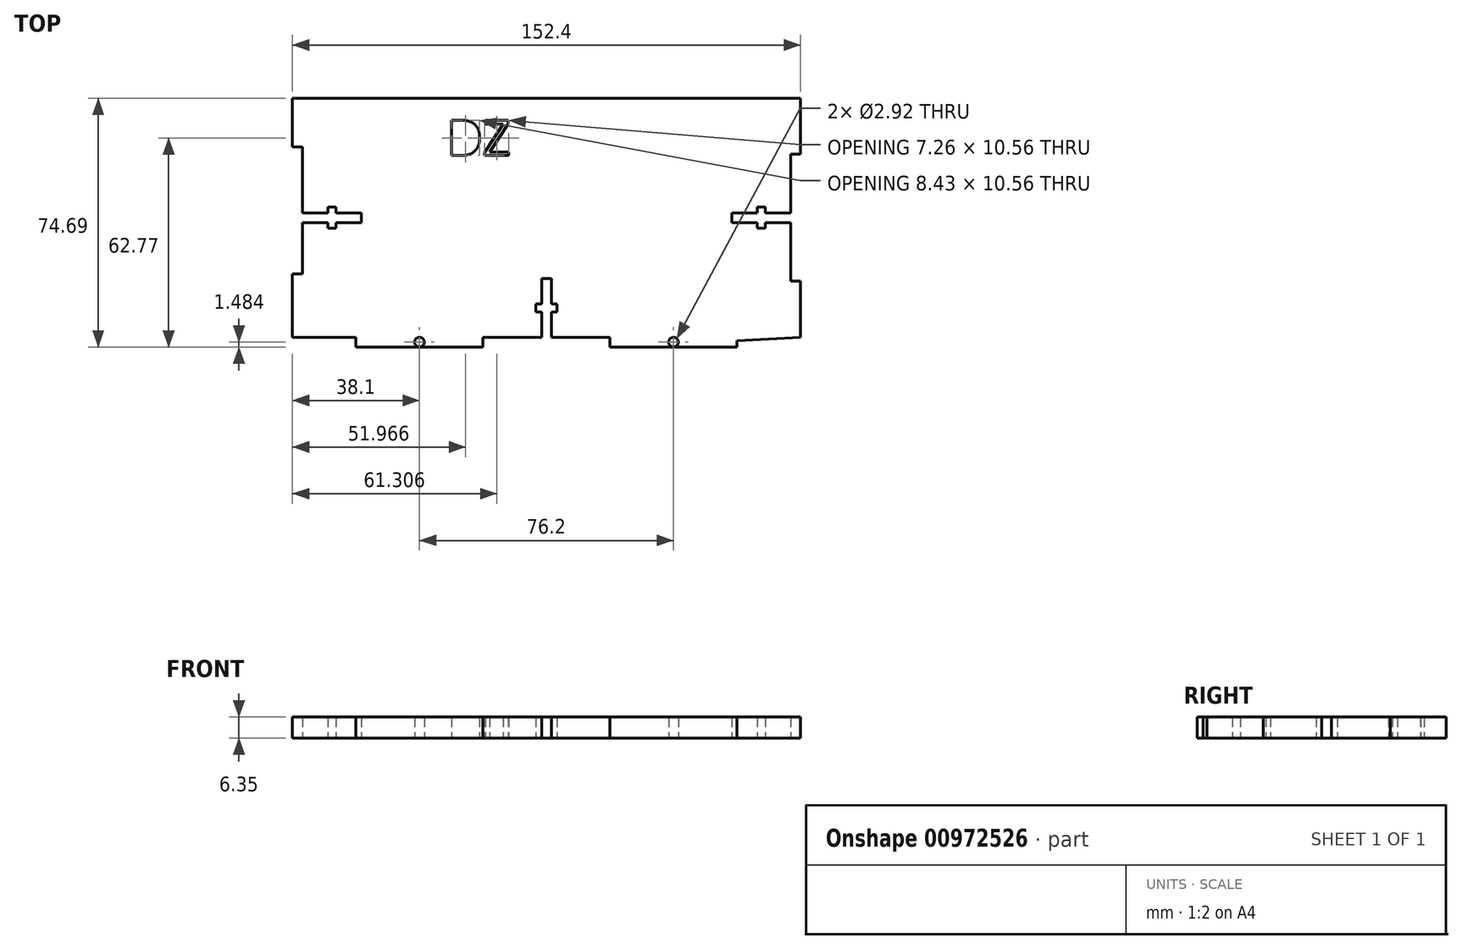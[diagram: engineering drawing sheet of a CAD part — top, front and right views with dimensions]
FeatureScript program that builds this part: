
annotation { "Feature Type Name" : "Feature", "Feature Type Description" : "" }
export const myFeature = defineFeature(function(context is Context, id is Id, definition is map)
    precondition{}
    {
        {
            var Q0;
            Q0=qCreatedBy(makeId("Top.planeOp"),FACE);
            var sketch = newSketch(context, id + "F0", { "sketchPlane" : qUnion([Q0])});
            skLineSegment(sketch, "E0.bottom", {"start": v(76.2, 35.86) * mm, "end": v(-76.2, 35.86) * mm});
            skLineSegment(sketch, "E0.top", {"start": v(76.2, -35.86) * mm, "end": v(57.15, -35.86) * mm});
            skLineSegment(sketch, "E0.left", {"start": v(76.2, 35.86) * mm, "end": v(76.2, 19.05) * mm});
            skLineSegment(sketch, "E0.right", {"start": v(-76.2, 35.86) * mm, "end": v(-76.2, 21.3) * mm});
            skPoint(sketch, "E0.middle", {"position": v(0, 0) * mm});
            skLineSegment(sketch, "E1", {"start": v(-57.15, -35.86) * mm, "end": v(-57.15, -38.83) * mm});
            skLineSegment(sketch, "E2", {"start": v(-57.15, -38.83) * mm, "end": v(-19.05, -38.83) * mm});
            skLineSegment(sketch, "E3", {"start": v(-19.05, -38.83) * mm, "end": v(-19.05, -35.86) * mm});
            skLineSegment(sketch, "E4", {"start": v(-19.05, -35.86) * mm, "end": v(-1.46, -35.86) * mm});
            skLineSegment(sketch, "E5", {"start": v(19.05, -35.86) * mm, "end": v(19.05, -38.83) * mm});
            skLineSegment(sketch, "E6", {"start": v(19.05, -38.83) * mm, "end": v(57.15, -38.83) * mm});
            skLineSegment(sketch, "E7", {"start": v(57.15, -38.83) * mm, "end": v(57.15, -35.86) * mm});
            skLineSegment(sketch, "E8", {"start": v(-38.1, -38.83) * mm, "end": v(-38.1, -35.86) * mm, "construction": true});
            skLineSegment(sketch, "E9", {"start": v(-57.15, -37.35) * mm, "end": v(-19.05, -37.35) * mm, "construction": true});
            skLineSegment(sketch, "E10", {"start": v(19.05, -37.35) * mm, "end": v(57.15, -37.35) * mm, "construction": true});
            skLineSegment(sketch, "E11", {"start": v(38.1, -38.83) * mm, "end": v(38.1, -38.1) * mm, "construction": true});
            skPoint(sketch, "E11.endSnap0", {"position": v(38.1, -37.35) * mm});
            skLineSegment(sketch, "E12", {"start": v(-1.46, -35.86) * mm, "end": v(-1.46, -28.24) * mm});
            skLineSegment(sketch, "E13", {"start": v(-1.46, -28.24) * mm, "end": v(-3.17, -28.24) * mm});
            skLineSegment(sketch, "E14", {"start": v(-3.17, -28.24) * mm, "end": v(-3.17, -25.83) * mm});
            skLineSegment(sketch, "E15", {"start": v(-3.17, -25.83) * mm, "end": v(-1.46, -25.83) * mm});
            skLineSegment(sketch, "E16", {"start": v(-1.46, -25.83) * mm, "end": v(-1.46, -18.2) * mm});
            skLineSegment(sketch, "E17", {"start": v(-1.46, -18.2) * mm, "end": v(1.46, -18.2) * mm});
            skLineSegment(sketch, "E18", {"start": v(1.46, -18.2) * mm, "end": v(1.46, -25.83) * mm});
            skLineSegment(sketch, "E19", {"start": v(1.46, -25.83) * mm, "end": v(3.18, -25.83) * mm});
            skLineSegment(sketch, "E20", {"start": v(3.17, -25.83) * mm, "end": v(3.17, -28.24) * mm});
            skLineSegment(sketch, "E21", {"start": v(3.18, -28.24) * mm, "end": v(1.46, -28.24) * mm});
            skLineSegment(sketch, "E22", {"start": v(1.46, -28.24) * mm, "end": v(1.46, -35.86) * mm});
            skLineSegment(sketch, "E23", {"start": v(-1.46, -39.34) * mm, "end": v(0, -39.34) * mm, "construction": true});
            skLineSegment(sketch, "E24", {"start": v(0, -39.34) * mm, "end": v(1.46, -39.34) * mm, "construction": true});
            skLineSegment(sketch, "E25", {"start": v(-1.46, -25.83) * mm, "end": v(0, -25.83) * mm, "construction": true});
            skLineSegment(sketch, "E26", {"start": v(0, -25.83) * mm, "end": v(1.46, -25.83) * mm, "construction": true});
            skLineSegment(sketch, "E27", {"start": v(-76.2, 21.3) * mm, "end": v(-73.23, 21.3) * mm});
            skLineSegment(sketch, "E28", {"start": v(-73.23, 21.3) * mm, "end": v(-73.23, 1.46) * mm});
            skLineSegment(sketch, "E29", {"start": v(-73.23, -16.8) * mm, "end": v(-76.2, -16.8) * mm});
            skLineSegment(sketch, "E30", {"start": v(76.2, 19.05) * mm, "end": v(73.23, 19.05) * mm});
            skLineSegment(sketch, "E31", {"start": v(73.23, 19.05) * mm, "end": v(73.23, 1.46) * mm});
            skLineSegment(sketch, "E32", {"start": v(73.23, -19.05) * mm, "end": v(76.2, -19.05) * mm});
            skLineSegment(sketch, "E33", {"start": v(-19.05, -38.83) * mm, "end": v(19.05, -38.83) * mm, "construction": true});
            skLineSegment(sketch, "E34", {"start": v(-74.71, 21.3) * mm, "end": v(-74.71, -16.8) * mm, "construction": true});
            skLineSegment(sketch, "E35", {"start": v(74.71, 19.05) * mm, "end": v(74.71, -19.05) * mm, "construction": true});
            skLineSegment(sketch, "E36", {"start": v(-73.23, 1.46) * mm, "end": v(-65.6, 1.46) * mm});
            skLineSegment(sketch, "E37", {"start": v(-65.6, 1.46) * mm, "end": v(-65.6, 3.17) * mm});
            skLineSegment(sketch, "E38", {"start": v(-65.6, 3.17) * mm, "end": v(-63.2, 3.17) * mm});
            skLineSegment(sketch, "E39", {"start": v(-63.2, 3.17) * mm, "end": v(-63.2, 1.46) * mm});
            skLineSegment(sketch, "E40", {"start": v(-63.2, 1.46) * mm, "end": v(-55.58, 1.46) * mm});
            skLineSegment(sketch, "E41", {"start": v(-55.58, 1.46) * mm, "end": v(-55.58, -1.46) * mm});
            skLineSegment(sketch, "E42", {"start": v(-55.58, -1.46) * mm, "end": v(-63.2, -1.46) * mm});
            skLineSegment(sketch, "E43", {"start": v(-63.2, -1.46) * mm, "end": v(-63.2, -3.18) * mm});
            skLineSegment(sketch, "E44", {"start": v(-63.2, -3.18) * mm, "end": v(-65.6, -3.18) * mm});
            skLineSegment(sketch, "E45", {"start": v(-65.6, -3.18) * mm, "end": v(-65.6, -1.46) * mm});
            skLineSegment(sketch, "E46", {"start": v(-65.6, -1.46) * mm, "end": v(-73.23, -1.46) * mm});
            skLineSegment(sketch, "E47", {"start": v(-63.2, 0) * mm, "end": v(-63.2, 1.46) * mm, "construction": true});
            skLineSegment(sketch, "E48", {"start": v(-63.2, 0) * mm, "end": v(-63.2, -1.46) * mm, "construction": true});
            skLineSegment(sketch, "E49.MirrorCS", {"start": v(65.6, 1.46) * mm, "end": v(65.6, -1.46) * mm, "construction": true});
            skLineSegment(sketch, "E50.MirrorCS", {"start": v(63.2, 3.17) * mm, "end": v(63.2, 1.46) * mm});
            skLineSegment(sketch, "E51.MirrorCS", {"start": v(65.6, 1.46) * mm, "end": v(65.6, 3.17) * mm});
            skLineSegment(sketch, "E52.MirrorCS", {"start": v(63.2, 0) * mm, "end": v(63.2, 1.46) * mm, "construction": true});
            skLineSegment(sketch, "E53.MirrorCS", {"start": v(65.6, 0) * mm, "end": v(65.6, -1.46) * mm});
            skLineSegment(sketch, "E54.MirrorCS", {"start": v(63.2, 0) * mm, "end": v(63.2, -1.46) * mm, "construction": true});
            skLineSegment(sketch, "E55.MirrorCS", {"start": v(65.6, 3.17) * mm, "end": v(63.2, 3.17) * mm});
            skLineSegment(sketch, "E56.MirrorCS", {"start": v(73.23, 1.46) * mm, "end": v(65.6, 1.46) * mm});
            skLineSegment(sketch, "E57.MirrorCS", {"start": v(63.2, 1.46) * mm, "end": v(55.58, 1.46) * mm});
            skLineSegment(sketch, "E58.MirrorCS", {"start": v(55.58, 1.46) * mm, "end": v(55.58, -1.46) * mm});
            skLineSegment(sketch, "E59.MirrorCS", {"start": v(55.58, -1.46) * mm, "end": v(63.2, -1.46) * mm});
            skLineSegment(sketch, "E60.MirrorCS", {"start": v(63.2, -1.46) * mm, "end": v(63.2, -3.18) * mm});
            skLineSegment(sketch, "E61.MirrorCS", {"start": v(63.2, -3.17) * mm, "end": v(65.6, -3.17) * mm});
            skLineSegment(sketch, "E62.MirrorCS", {"start": v(65.6, -1.46) * mm, "end": v(73.23, -1.46) * mm});
            skLineSegment(sketch, "E63.MirrorCS", {"start": v(65.6, -3.18) * mm, "end": v(65.6, -1.46) * mm});
            skLineSegment(sketch, "E64", {"start": v(-76.2, -35.86) * mm, "end": v(-76.2, -47.97) * mm, "construction": true});
            skCircle(sketch, "E65", {"center": v(-38.1, -37.35) * mm, "radius": 1.46 * mm});
            skLineSegment(sketch, "E66", {"start": v(-38.1, -35.86) * mm, "end": v(-38.1, -34.57) * mm, "construction": true});
            skLineSegment(sketch, "E67", {"start": v(38.1, -38.1) * mm, "end": v(38.1, -36.3) * mm, "construction": true});
            skCircle(sketch, "E68", {"center": v(38.1, -37.35) * mm, "radius": 1.46 * mm});
            skText(sketch, "E69", { "text": "DZ\n", "fontName": "OpenSans-Regular.ttf"});
            skPoint(sketch, "E70.end.orphan", {"position": v(-73.23, -35.86) * mm});
            skLineSegment(sketch, "E71.trimOffspring", {"start": v(-76.2, -16.8) * mm, "end": v(-76.2, -35.86) * mm});
            skLineSegment(sketch, "E72.trimOffspring", {"start": v(-73.23, -1.46) * mm, "end": v(-73.23, -16.8) * mm});
            skPoint(sketch, "E73.start.orphan", {"position": v(-65.6, 0) * mm});
            skLineSegment(sketch, "E74.trimOffspring", {"start": v(-57.15, -35.86) * mm, "end": v(-76.2, -35.86) * mm});
            skLineSegment(sketch, "E75.trimOffspring", {"start": v(38.1, -38.1) * mm, "end": v(76.2, -35.86) * mm});
            skLineSegment(sketch, "E76", {"start": v(-1.46, -27.87) * mm, "end": v(1.46, -27.87) * mm, "construction": true});
            skLineSegment(sketch, "E77.trimOffspring", {"start": v(-1.46, -35.86) * mm, "end": v(-19.05, -35.86) * mm});
            skLineSegment(sketch, "E78", {"start": v(19.05, -35.86) * mm, "end": v(1.46, -35.86) * mm});
            skLineSegment(sketch, "E79.trimOffspring", {"start": v(76.2, -19.05) * mm, "end": v(76.2, -35.86) * mm});
            skPoint(sketch, "E80.MirrorCS.end.orphan", {"position": v(65.6, -1.46) * mm});
            skPoint(sketch, "E80.MirrorCS.start.orphan", {"position": v(65.6, 0) * mm});
            skPoint(sketch, "E81.MirrorCS.end.orphan", {"position": v(65.6, 1.46) * mm});
            skLineSegment(sketch, "E82.trimOffspring", {"start": v(73.23, -1.46) * mm, "end": v(73.23, -19.05) * mm});
            const initialGuessF0  = {"E69": [-0.0299, 0.01866, 1, 0, 0.01065]};
            skSetInitialGuess(sketch, initialGuessF0);
            skSolve(sketch);
        }
        {
            var Q0;
            {var subQ4=sQuery(id+"F0.wireOp",EDGE,"E30");Q0=makeQuery(id+"F0.imprint","IMPRINT",FACE,{"disambiguationData":[TD([[makeQuery(id+"F0.imprint","IMPRINT",EDGE,{"derivedFrom":subQ4}),-1.0]])]});}
            var Q1;
            {var subQ0=sQuery(id+"F0.wireOp",EDGE,"E0.right");Q1=makeQuery(id+"F0.imprint","IMPRINT",FACE,{"disambiguationData":[TD([[makeQuery(id+"F0.imprint","IMPRINT",EDGE,{"derivedFrom":subQ0}),1.0]])]});}
            var Q2;
            {var subQ4=sQuery(id+"F0.wireOp",EDGE,"E29");Q2=makeQuery(id+"F0.imprint","IMPRINT",FACE,{"disambiguationData":[TD([[makeQuery(id+"F0.imprint","IMPRINT",EDGE,{"derivedFrom":subQ4}),1.0]])]});}
            var Q3;
            {var subQ3=sQuery(id+"F0.wireOp",EDGE,"E32");Q3=makeQuery(id+"F0.imprint","IMPRINT",FACE,{"disambiguationData":[TD([[makeQuery(id+"F0.imprint","IMPRINT",EDGE,{"derivedFrom":subQ3}),-1.0]])]});}
            var Q4;
            {var subQ1=sQuery(id+"F0.wireOp",EDGE,"E1");var subQ5=sQuery(id+"F0.wireOp",EDGE,"E2");var subQ6=makeQuery(id+"F0.imprint","INTERSECT",VERTEX,{"derivedFrom":[subQ1,subQ5]});Q4=makeQuery(id+"F0.imprint","IMPRINT",FACE,{"disambiguationData":[TD([[makeQuery(id+"F0.imprint","IMPRINT",EDGE,{"disambiguationData":[TD([[subQ6,1.0]])],"derivedFrom":subQ1}),1.0]])]});}
            var Q5;
            {var subQ1=sQuery(id+"F0.wireOp",EDGE,"E3");var subQ6=sQuery(id+"F0.wireOp",EDGE,"E2");var subQ9=makeQuery(id+"F0.imprint","INTERSECT",VERTEX,{"derivedFrom":[subQ6,subQ1]});Q5=makeQuery(id+"F0.imprint","IMPRINT",FACE,{"disambiguationData":[TD([[makeQuery(id+"F0.imprint","IMPRINT",EDGE,{"disambiguationData":[TD([[subQ9,1.0]])],"derivedFrom":subQ6}),1.0]])]});}
            var Q6;
            {var subQ1=sQuery(id+"F0.wireOp",EDGE,"E6");var subQ5=sQuery(id+"F0.wireOp",EDGE,"E5");var subQ6=makeQuery(id+"F0.imprint","INTERSECT",VERTEX,{"derivedFrom":[subQ5,subQ1]});Q6=makeQuery(id+"F0.imprint","IMPRINT",FACE,{"disambiguationData":[TD([[makeQuery(id+"F0.imprint","IMPRINT",EDGE,{"disambiguationData":[TD([[subQ6,1.0]])],"derivedFrom":subQ5}),1.0]])]});}
            var Q7;
            {var subQ1=sQuery(id+"F0.wireOp",EDGE,"E6");var subQ6=sQuery(id+"F0.wireOp",EDGE,"E7");var subQ9=makeQuery(id+"F0.imprint","INTERSECT",VERTEX,{"derivedFrom":[subQ1,subQ6]});Q7=makeQuery(id+"F0.imprint","IMPRINT",FACE,{"disambiguationData":[TD([[makeQuery(id+"F0.imprint","IMPRINT",EDGE,{"disambiguationData":[TD([[subQ9,1.0]])],"derivedFrom":subQ1}),1.0]])]});}
            var Q8;
            {var subQ1=sQuery(id+"F0.wireOp",EDGE,"E1");var subQ6=sQuery(id+"F0.wireOp",EDGE,"E0.top");var subQ9=makeQuery(id+"F0.imprint","INTERSECT",VERTEX,{"derivedFrom":[subQ6,subQ1]});Q8=makeQuery(id+"F0.imprint","IMPRINT",FACE,{"disambiguationData":[TD([[makeQuery(id+"F0.imprint","IMPRINT",EDGE,{"disambiguationData":[TD([[subQ9,1.0]])],"derivedFrom":subQ6}),1.0]])]});}
            var Q9;
            {var subQ5=sQuery(id+"F0.wireOp",EDGE,"E5");var subQ7=sQuery(id+"F0.wireOp",EDGE,"E10");var subQ8=makeQuery(id+"F0.imprint","INTERSECT",VERTEX,{"derivedFrom":[subQ5,subQ7]});Q9=makeQuery(id+"F0.imprint","IMPRINT",FACE,{"disambiguationData":[TD([[makeQuery(id+"F0.imprint","IMPRINT",EDGE,{"disambiguationData":[TD([[subQ8,-1.0]])],"derivedFrom":subQ7}),1.0]])]});}
            var Q10;
            {var subQ1=sQuery(id+"F0.wireOp",EDGE,"B1DGfkQQ-ObTF-AqKt-jh10-ahFj8GnIkkbg");var subQ6=sQuery(id+"F0.wireOp",EDGE,"E7");var subQ9=makeQuery(id+"F0.imprint","INTERSECT",VERTEX,{"derivedFrom":[subQ6,subQ1]});Q10=makeQuery(id+"F0.imprint","IMPRINT",FACE,{"disambiguationData":[TD([[makeQuery(id+"F0.imprint","IMPRINT",EDGE,{"disambiguationData":[TD([[subQ9,1.0]])],"derivedFrom":subQ6}),1.0]])]});}
            var Q11;
            {var subQ18=sQuery(id+"F0.wireOp",EDGE,"E12");Q11=makeQuery(id+"F0.imprint","IMPRINT",FACE,{"disambiguationData":[TD([[makeQuery(id+"F0.imprint","IMPRINT",EDGE,{"derivedFrom":subQ18}),1.0]])]});}
            var Q12;
            {var subQ0=sQuery(id+"F0.wireOp",EDGE,"E3");var subQ5=sQuery(id+"F0.wireOp",EDGE,"E9");var subQ6=makeQuery(id+"F0.imprint","INTERSECT",VERTEX,{"derivedFrom":[subQ0,subQ5]});Q12=makeQuery(id+"F0.imprint","IMPRINT",FACE,{"disambiguationData":[TD([[makeQuery(id+"F0.imprint","IMPRINT",EDGE,{"disambiguationData":[TD([[subQ6,1.0]])],"derivedFrom":subQ5}),1.0]])]});}
            extrude(context, id + "F1", {"entities" : qUnion([Q0, Q1, Q2, Q3, Q4, Q5, Q6, Q7, Q8, Q9, Q10, Q11, Q12]), "depth" : 6.35 * mm, "offsetDistance" : 25.4 * mm});
        }
    });
